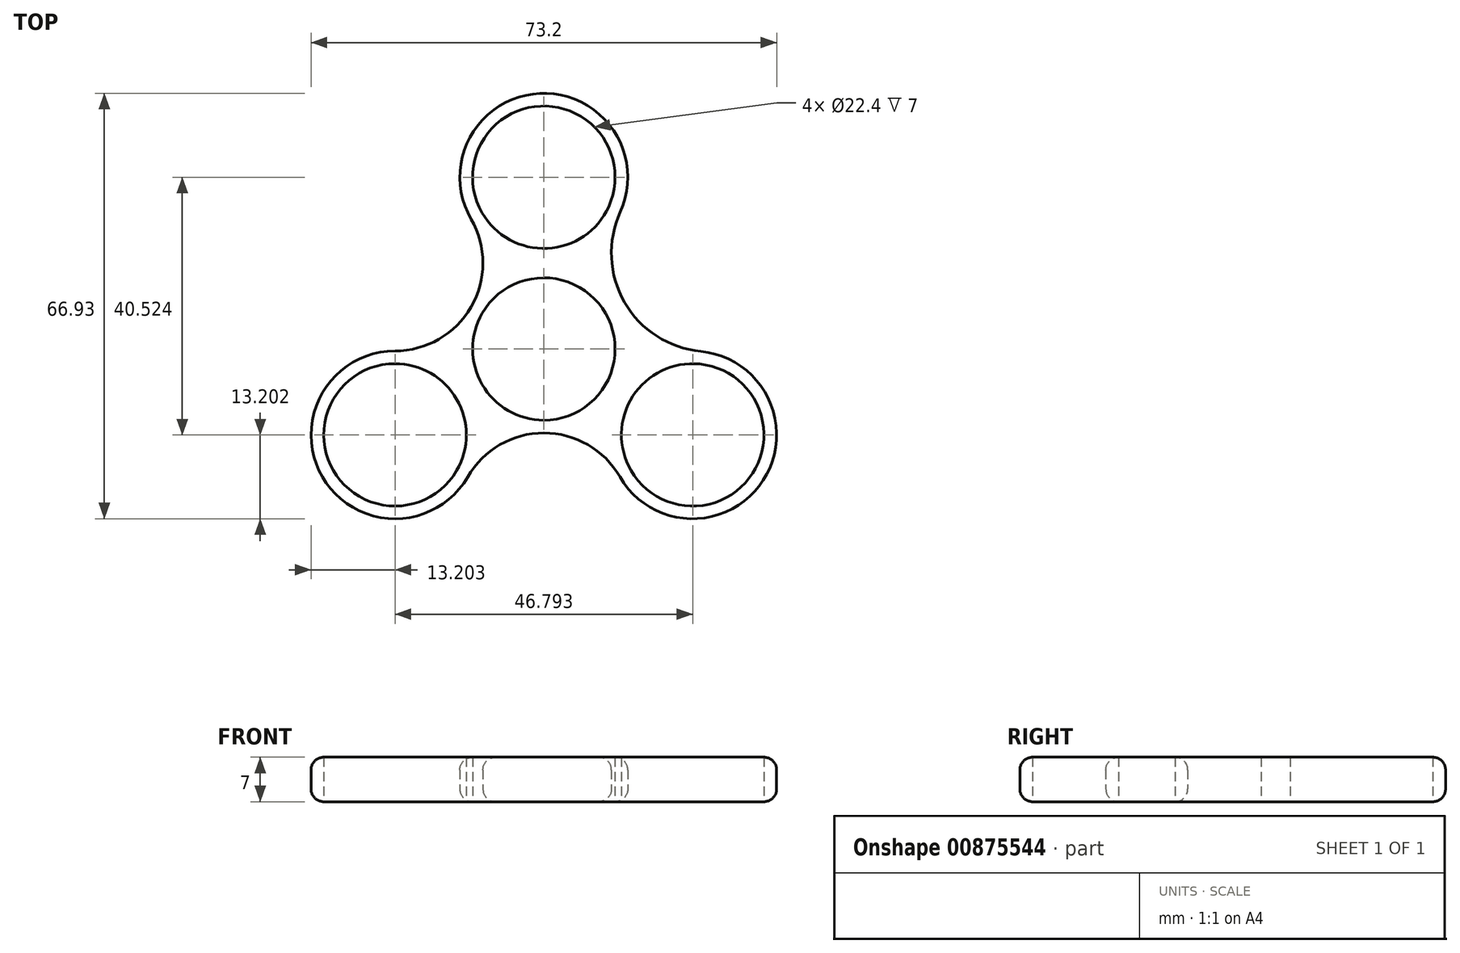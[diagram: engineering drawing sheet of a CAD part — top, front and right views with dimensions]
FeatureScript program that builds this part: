
annotation { "Feature Type Name" : "Feature", "Feature Type Description" : "" }
export const myFeature = defineFeature(function(context is Context, id is Id, definition is map)
    precondition{}
    {
        {
            var Q0;
            Q0=qCreatedBy(makeId("Top.planeOp"),FACE);
            var sketch = newSketch(context, id + "F0", { "sketchPlane" : qUnion([Q0])});
            skCircle(sketch, "E0", {"center": v(0, 0) * mm, "radius": 11.2 * mm});
            skCircle(sketch, "E1", {"center": v(0, 27.02) * mm, "radius": 11.2 * mm});
            skArc(sketch, "E2", {"start": v(12.01, 21.55) * mm, "mid": v(-0.64, 40.2) * mm, "end": v(-11.43, 20.42) * mm});
            skArc(sketch, "E3.1.0", {"start": v(-23.4, -0.3) * mm, "mid": v(-34.83, -20.1) * mm, "end": v(-11.97, -20.1) * mm});
            skCircle(sketch, "E3.1.1", {"center": v(-23.4, -13.5) * mm, "radius": 11.2 * mm});
            skArc(sketch, "E3.2.0", {"start": v(11.97, -20.1) * mm, "mid": v(34.5, -20.65) * mm, "end": v(24.67, -0.37) * mm});
            skCircle(sketch, "E3.2.1", {"center": v(23.4, -13.5) * mm, "radius": 11.2 * mm});
            skLineSegment(sketch, "E4", {"start": v(0, 0) * mm, "end": v(23.4, -13.5) * mm, "construction": true});
            skLineSegment(sketch, "E5", {"start": v(0, 27.02) * mm, "end": v(0, 0) * mm, "construction": true});
            skLineSegment(sketch, "E6", {"start": v(-23.4, -13.5) * mm, "end": v(0, 0) * mm, "construction": true});
            skArc(sketch, "E7.1.0", {"start": v(-23.4, -0.3) * mm, "mid": v(-11.43, 6.6) * mm, "end": v(-11.43, 20.42) * mm});
            skArc(sketch, "E7.2.0", {"start": v(11.97, -20.1) * mm, "mid": v(0, -13.2) * mm, "end": v(-11.97, -20.1) * mm});
            skLineSegment(sketch, "E8", {"start": v(0, 15.82) * mm, "end": v(0, 38.22) * mm, "construction": true});
            skLineSegment(sketch, "E9.anchor1", {"start": v(0, 0) * mm, "end": v(0, 27.02) * mm, "construction": true});
            skLineSegment(sketch, "E9.anchor2", {"start": v(0, 0) * mm, "end": v(-23.4, -13.5) * mm, "construction": true});
            skArc(sketch, "E10", {"start": v(12.01, 21.55) * mm, "mid": v(12.7, 7.33) * mm, "end": v(24.67, -0.37) * mm});
            skSolve(sketch);
        }
        {
            var Q0;
            Q0 = qSketchRegion(id + "F0", true);
            extrude(context, id + "F1", {"entities" : qUnion([Q0]), "depth" : 7 * mm, "offsetDistance" : 25 * mm});
        }
        {
            var Q0;
            Q0=makeQuery(id+"F1.opExtrude","CAP_EDGE",EDGE,{"disambiguationData":[OSD([sQuery(id+"F0.wireOp",EDGE,"E3.1.0")])],"isStart":false});
            var Q1;
            Q1=makeQuery(id+"F1.opExtrude","CAP_EDGE",EDGE,{"disambiguationData":[OSD([sQuery(id+"F0.wireOp",EDGE,"E7.2.0")])],"isStart":false});
            var Q2;
            Q2=makeQuery(id+"F1.opExtrude","CAP_EDGE",EDGE,{"disambiguationData":[OSD([sQuery(id+"F0.wireOp",EDGE,"E3.2.0")])],"isStart":false});
            var Q3;
            Q3=makeQuery(id+"F1.opExtrude","CAP_EDGE",EDGE,{"disambiguationData":[OSD([sQuery(id+"F0.wireOp",EDGE,"m5yOy5yj-LvNj-hlmw-sKo6-v5u0e3Bkxz3A")])],"isStart":false});
            var Q4;
            Q4=makeQuery(id+"F1.opExtrude","CAP_EDGE",EDGE,{"disambiguationData":[OSD([sQuery(id+"F0.wireOp",EDGE,"E2")])],"isStart":false});
            var Q5;
            Q5=makeQuery(id+"F1.opExtrude","CAP_EDGE",EDGE,{"disambiguationData":[OSD([sQuery(id+"F0.wireOp",EDGE,"E7.1.0")])],"isStart":false});
            var Q6;
            Q6=makeQuery(id+"F1.opExtrude","CAP_EDGE",EDGE,{"disambiguationData":[OSD([sQuery(id+"F0.wireOp",EDGE,"E3.2.0")])],"isStart":true});
            var Q7;
            Q7=makeQuery(id+"F1.opExtrude","CAP_EDGE",EDGE,{"disambiguationData":[OSD([sQuery(id+"F0.wireOp",EDGE,"m5yOy5yj-LvNj-hlmw-sKo6-v5u0e3Bkxz3A")])],"isStart":true});
            var Q8;
            Q8=makeQuery(id+"F1.opExtrude","CAP_EDGE",EDGE,{"disambiguationData":[OSD([sQuery(id+"F0.wireOp",EDGE,"E2")])],"isStart":true});
            var Q9;
            Q9=makeQuery(id+"F1.opExtrude","CAP_EDGE",EDGE,{"disambiguationData":[OSD([sQuery(id+"F0.wireOp",EDGE,"E7.1.0")])],"isStart":true});
            var Q10;
            Q10=makeQuery(id+"F1.opExtrude","CAP_EDGE",EDGE,{"disambiguationData":[OSD([sQuery(id+"F0.wireOp",EDGE,"E3.1.0")])],"isStart":true});
            var Q11;
            Q11=makeQuery(id+"F1.opExtrude","CAP_EDGE",EDGE,{"disambiguationData":[OSD([sQuery(id+"F0.wireOp",EDGE,"E7.2.0")])],"isStart":true});
            fillet(context, id + "F2", {"entities" : qUnion([Q0, Q1, Q2, Q3, Q4, Q5, Q6, Q7, Q8, Q9, Q10, Q11]), "radius" : 2 * mm, "tangentPropagation" : true, "allowEdgeOverflow" : false});
        }
    });
